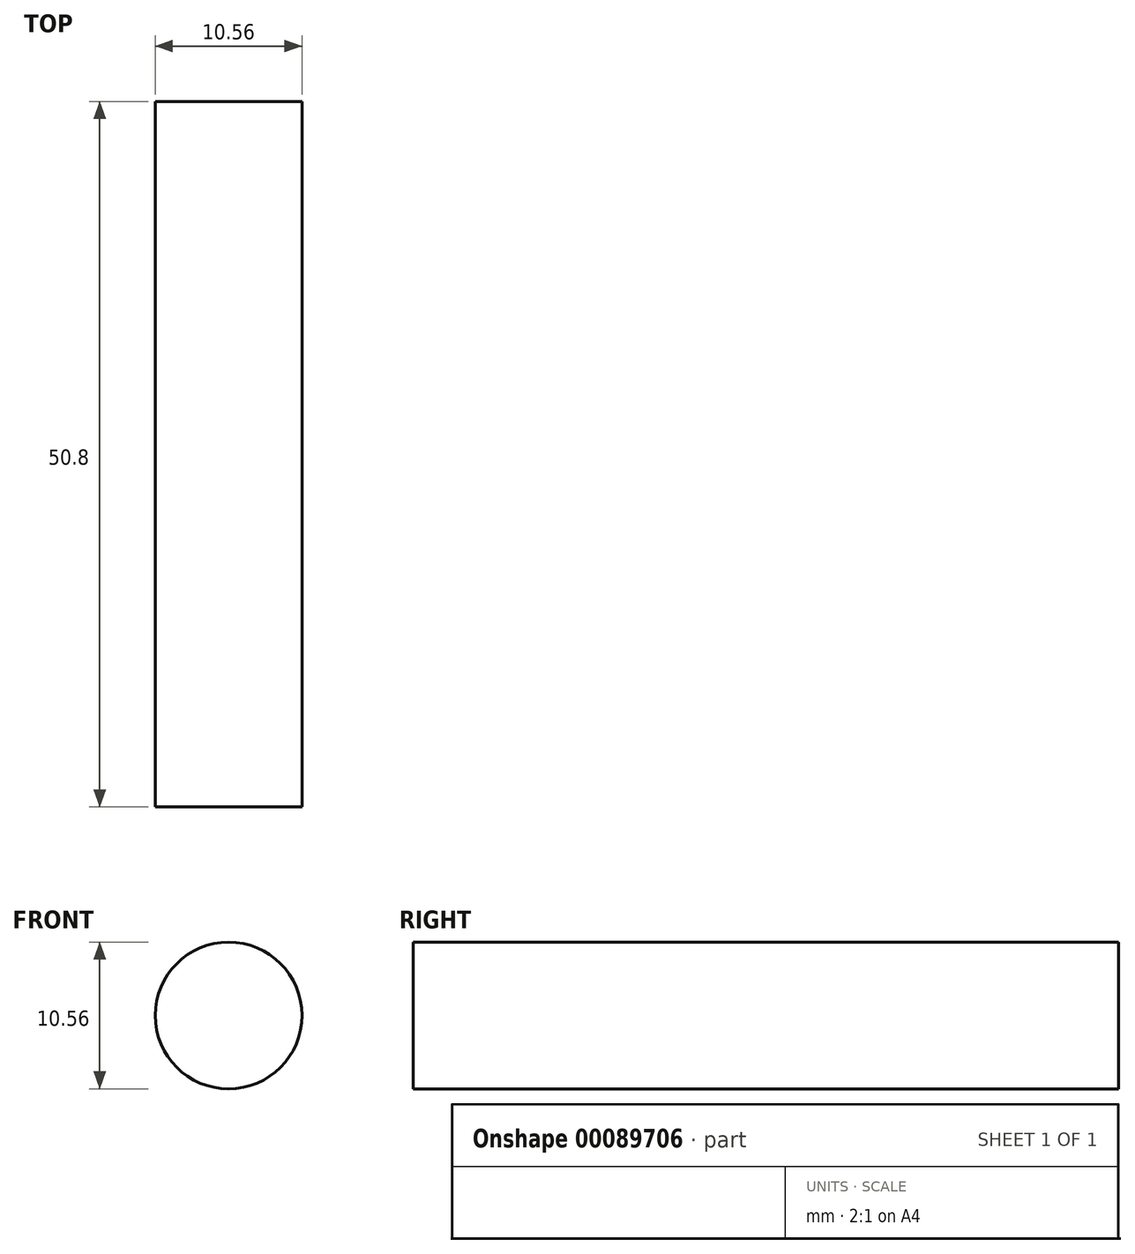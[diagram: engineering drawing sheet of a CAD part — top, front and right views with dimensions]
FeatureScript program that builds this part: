
annotation { "Feature Type Name" : "Feature", "Feature Type Description" : "" }
export const myFeature = defineFeature(function(context is Context, id is Id, definition is map)
    precondition{}
    {
        {
            var Q0;
            Q0=qCreatedBy(makeId("Front.planeOp"),FACE);
            var sketch = newSketch(context, id + "F0", { "sketchPlane" : qUnion([Q0])});
            skCircle(sketch, "E0", {"center": v(0, 0) * mm, "radius": 5.28 * mm});
            skSolve(sketch);
        }
        {
            var Q0;
            Q0=makeQuery(id+"F0.imprint","IMPRINT",FACE,{"disambiguationData":[TD([[makeQuery(id+"F0.imprint","IMPRINT",EDGE,{"derivedFrom":sQuery(id+"F0.wireOp",EDGE,"E0")}),1.0]])]});
            extrude(context, id + "F1", {"entities" : qUnion([Q0]), "depth" : 50.8 * mm});
        }
    });
